# Revit family: STH9740BR_27_PTO_27_STH9740BR_30_PTO_30
name_source: partatom
category: Luminárias
units: mm (PartAtom-declared; Revit-internal decimal feet)

## family parameters
Compartilhado = Não
Corte com vazios quando carregada = Não
Cota do conector redondo = Utilizar diâmetro
Fonte luminosa = Sim
Hospedeiro = Parede
Manter orientação da anotação = Não
Número OmniClass = 23.80.70.00
Ponto de cálculo do ambiente = Não
Sempre na vertical = Sim
Tipo de parte = Normal
Título OmniClass = Lighting

## types (4) — shared parameters
Comprimento = 0.42 m
Dimerização = Não dimerizável
Emitir do comprimento da linha = 0.61 m
Fabricante = Stella
Filtro de cor = 16777215
Grau de proteção (IP) = IP65
IRC (Índice de reprodução de cores) = >80
Largura = 0.12 m
Modelo = Reflex
Potência = 12 W
Profundidade = 0.03 m
Tamanho do símbolo da fonte luminosa = 0.61 m
Tensão Elétrica = 100V-240V
Troca de temperatura da cor de lâmpada com esmaecimento = <Nenhum>
URL = https://stella.com.br
Ângulo de Abertura = 110°/110°
zero-valued in all types: Elevação padrão

## per-type parameters (varying)
| type | Estrutura | Fluxo Luminoso | Fonte Luminosa_STH9740_2700K | Fonte Luminosa_STH9740_3000K | Luminoso | Referência | Temperatura da cor (K) |
| STH9740BR/30 - BRANCO - BIVOLT - 3000K - 1100lm | Al Branco | 1100 lm | Não | Sim | Luminoso - 3000K | STH9740BR/30 | 3000 K |
| STH9740BR/27 - BRANCO - BIVOLT - 2700K - 1050lm | Al Branco | 1050 lm | Sim | Não | Luminoso - 2700K | STH9740BR/27 | 2700 K |
| STH9740PTO/27 - PRETO - BIVOLT - 2700K - 800lm | Al - Preto | 800 lm | Sim | Não | Luminoso - 2700K | STH9740PTO/27 | 2700 K |
| STH9740PTO/30 - PRETO - BIVOLT - 3000K - 850lm | Al - Preto | 850 lm | Não | Sim | Luminoso - 3000K | STH9740PTO/30 | 3000 K |
